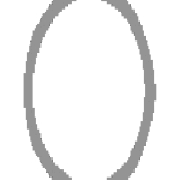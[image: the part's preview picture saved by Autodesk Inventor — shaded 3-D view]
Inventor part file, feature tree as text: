
AUTODESK INVENTOR PART (.ipt)
format: ipt  version: 2021 (Build 250183000, 183)  size: 110,592 bytes
history: native  units: in
note: dims shown in document units (in); Inventor stores cm internally (conversion verified against a paired STEP export)
features: other x4, sketch x3, plane x1
ambient origin geometry x8: Origin, YZ Plane, XZ Plane, XY Plane, X Axis, Y Axis, Z Axis, Center Point
bodies: Solid1 (feature_tree), Body (feature_tree)
feature tree (8):
  other  "Driven Length"
  other  "Frame Generator"
  other  "Start Plane"
  other  "End Plane"
  sketch  "Sketch"  dims[d2=12.0in d4=-0.0in d5=12.0in d6=0.12in d7=0.0in d8=90.0deg d9=12.0in]
  sketch  "Sketch2"  dims[d0=1.0in]
  plane  "Work Plane3"
  sketch  "Sketch3"  dims[d1=0.065in]
